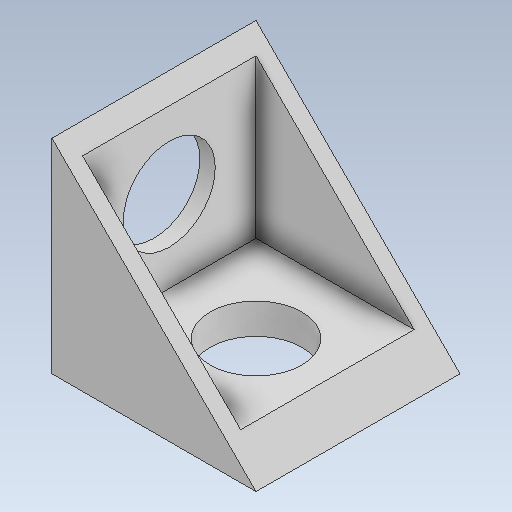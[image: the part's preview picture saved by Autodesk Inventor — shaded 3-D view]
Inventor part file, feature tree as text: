
AUTODESK INVENTOR PART (.ipt)
format: ipt  version: 2023 (Build 270158000, 158)  size: 124,928 bytes
history: native  units: in
note: dims shown in document units (in); Inventor stores cm internally (conversion verified against a paired STEP export)
features: sketch x5, other x3
ambient origin geometry x8: Origin, YZ Plane, XZ Plane, XY Plane, X Axis, Y Axis, Z Axis, Center Point
bodies: Solid1 (feature_tree)
feature tree (8):
  other  "CH-1-01-Cornerbracket1.ipt"
  other  "Solid1::CH-1-01-Cornerbracket1.ipt"
  other  "TaggingFeature1"
  sketch  "Sketch1"  dims[d0=0.3937in]
  sketch  "Sketch2"
  sketch  "Sketch6"
  sketch  "Sketch7"
  sketch  "Sketch8"
